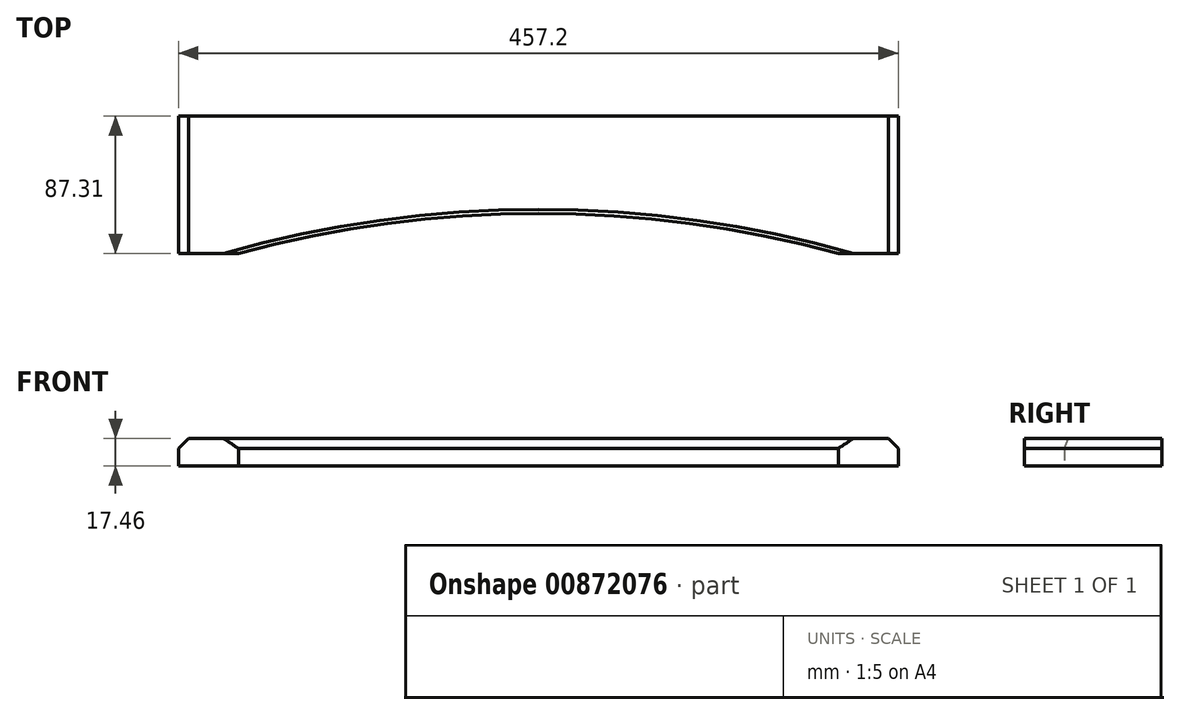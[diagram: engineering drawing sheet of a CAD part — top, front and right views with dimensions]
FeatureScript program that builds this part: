
annotation { "Feature Type Name" : "Feature", "Feature Type Description" : "" }
export const myFeature = defineFeature(function(context is Context, id is Id, definition is map)
    precondition{}
    {
        {
            var Q0;
            Q0=qCreatedBy(makeId("Top.planeOp"),FACE);
            var sketch = newSketch(context, id + "F0", { "sketchPlane" : qUnion([Q0])});
            skLineSegment(sketch, "E0.bottom", {"start": v(0, 0) * mm, "end": v(38.1, 0) * mm});
            skLineSegment(sketch, "E0.top", {"start": v(0, 87.31) * mm, "end": v(457.2, 87.31) * mm});
            skLineSegment(sketch, "E0.left", {"start": v(0, 0) * mm, "end": v(0, 87.31) * mm});
            skLineSegment(sketch, "E0.right", {"start": v(457.2, 0) * mm, "end": v(457.2, 87.31) * mm});
            skLineSegment(sketch, "E1", {"start": v(38.1, 16.63) * mm, "end": v(38.1, -30.86) * mm, "construction": true});
            skLineSegment(sketch, "E2", {"start": v(419.1, 20.9) * mm, "end": v(419.1, -35.43) * mm, "construction": true});
            skLineSegment(sketch, "E3", {"start": v(38.1, 0) * mm, "end": v(419.1, 0) * mm, "construction": true});
            skLineSegment(sketch, "E4", {"start": v(419.1, 0) * mm, "end": v(457.2, 0) * mm});
            skLineSegment(sketch, "E5", {"start": v(228.6, 0) * mm, "end": v(228.6, 25.4) * mm, "construction": true});
            skArc(sketch, "E6", {"start": v(419.1, 0) * mm, "mid": v(228.6, 25.4) * mm, "end": v(38.1, 0) * mm});
            skSolve(sketch);
        }
        {
            var Q0;
            Q0=qSketchRegion(id+"F0",true);
            extrude(context, id + "F1", {"entities" : qUnion([Q0]), "depth" : 17.46 * mm});
        }
        {
            var Q0;
            Q0=makeQuery(id+"F1.opExtrude","CAP_EDGE",EDGE,{"disambiguationData":[OSD([sQuery(id+"F0.wireOp",EDGE,"E0.left")])],"isStart":false});
            var Q1;
            Q1=makeQuery(id+"F1.opExtrude","CAP_EDGE",EDGE,{"disambiguationData":[OSD([sQuery(id+"F0.wireOp",EDGE,"E0.right")])],"isStart":false});
            chamfer(context, id + "F2", {"entities" : qUnion([Q0, Q1]), "width" : 6.35 * mm, "tangentPropagation" : true});
        }
        {
            var Q0;
            Q0=makeQuery(id+"F1.opExtrude","CAP_EDGE",EDGE,{"disambiguationData":[OSD([sQuery(id+"F0.wireOp",EDGE,"E6")])],"isStart":false});
            chamfer(context, id + "F3", {"entities" : qUnion([Q0]), "chamferType" : ChamferType.TWO_OFFSETS, "width1" : 6.35 * mm, "oppositeDirection" : false, "width2" : 2.54 * mm, "tangentPropagation" : true});
        }
    });
